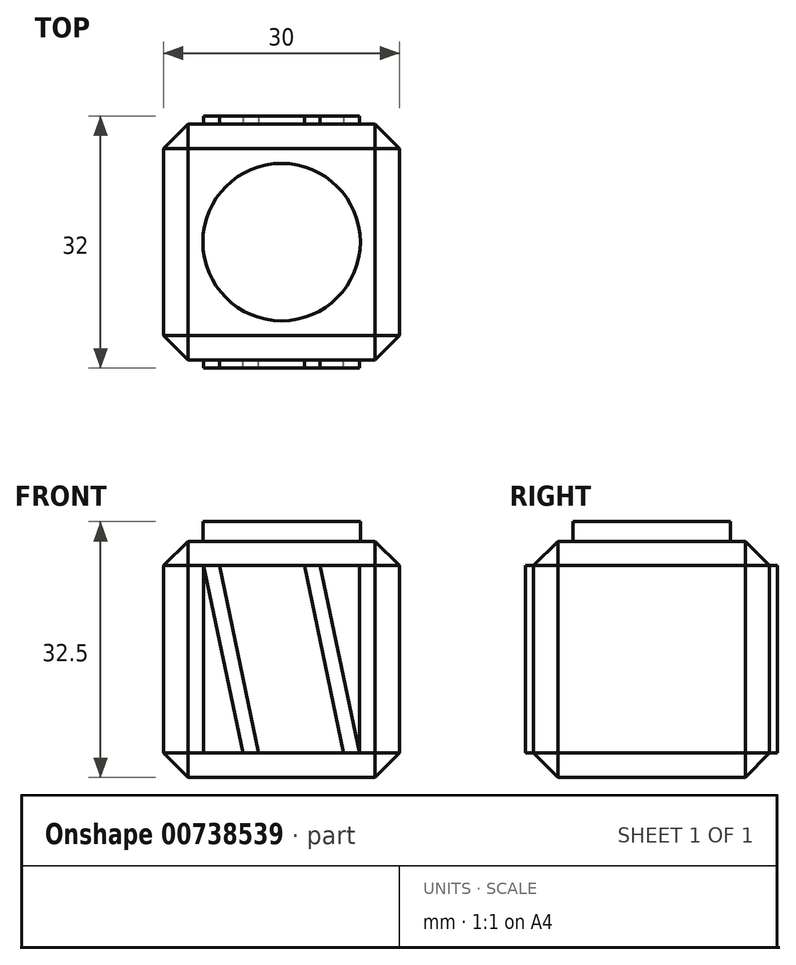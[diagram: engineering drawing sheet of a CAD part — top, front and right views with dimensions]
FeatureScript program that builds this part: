
annotation { "Feature Type Name" : "Feature", "Feature Type Description" : "" }
export const myFeature = defineFeature(function(context is Context, id is Id, definition is map)
    precondition{}
    {
        {
            var Q0;
            Q0=qCreatedBy(makeId("Top.planeOp"),FACE);
            var sketch = newSketch(context, id + "F0", { "sketchPlane" : qUnion([Q0])});
            skLineSegment(sketch, "E0", {"start": v(15, 15) * mm, "end": v(15, -15) * mm});
            skLineSegment(sketch, "E1", {"start": v(15, -15) * mm, "end": v(-15, -15) * mm});
            skLineSegment(sketch, "E2", {"start": v(-15, -15) * mm, "end": v(-15, 15) * mm});
            skLineSegment(sketch, "E3", {"start": v(-15, 15) * mm, "end": v(15, 15) * mm});
            skSolve(sketch);
        }
        {
            var Q0;
            Q0 = qSketchRegion(id + "F0", true);
            extrude(context, id + "F1", {"entities" : qUnion([Q0]), "depth" : 30 * mm, "offsetDistance" : 25 * mm});
        }
        {
            var Q0;
            Q0=makeQuery(id+"F1.opExtrude","CAP_EDGE",EDGE,{"disambiguationData":[OSD([sQuery(id+"F0.wireOp",EDGE,"E1")])],"isStart":false});
            var Q1;
            Q1=makeQuery(id+"F1.opExtrude","CAP_EDGE",EDGE,{"disambiguationData":[OSD([sQuery(id+"F0.wireOp",EDGE,"E0")])],"isStart":false});
            var Q2;
            Q2=makeQuery(id+"F1.opExtrude","SWEPT_EDGE",EDGE,{"disambiguationData":[OSD([sQuery(id+"F0.wireOp",EDGE,"E0"),sQuery(id+"F0.wireOp",EDGE,"E1")])]});
            var Q3;
            Q3=makeQuery(id+"F1.opExtrude","CAP_EDGE",EDGE,{"disambiguationData":[OSD([sQuery(id+"F0.wireOp",EDGE,"E2")])],"isStart":true});
            var Q4;
            Q4=makeQuery(id+"F1.opExtrude","CAP_EDGE",EDGE,{"disambiguationData":[OSD([sQuery(id+"F0.wireOp",EDGE,"E3")])],"isStart":true});
            var Q5;
            Q5=makeQuery(id+"F1.opExtrude","SWEPT_EDGE",EDGE,{"disambiguationData":[OSD([sQuery(id+"F0.wireOp",EDGE,"E2"),sQuery(id+"F0.wireOp",EDGE,"E3")])]});
            var Q6;
            Q6=makeQuery(id+"F1.opExtrude","CAP_EDGE",EDGE,{"disambiguationData":[OSD([sQuery(id+"F0.wireOp",EDGE,"E3")])],"isStart":false});
            var Q7;
            Q7=makeQuery(id+"F1.opExtrude","SWEPT_EDGE",EDGE,{"disambiguationData":[OSD([sQuery(id+"F0.wireOp",EDGE,"E0"),sQuery(id+"F0.wireOp",EDGE,"E3")])]});
            var Q8;
            Q8=makeQuery(id+"F1.opExtrude","SWEPT_EDGE",EDGE,{"disambiguationData":[OSD([sQuery(id+"F0.wireOp",EDGE,"E1"),sQuery(id+"F0.wireOp",EDGE,"E2")])]});
            var Q9;
            Q9=makeQuery(id+"F1.opExtrude","CAP_EDGE",EDGE,{"disambiguationData":[OSD([sQuery(id+"F0.wireOp",EDGE,"E1")])],"isStart":true});
            var Q10;
            Q10=makeQuery(id+"F1.opExtrude","CAP_EDGE",EDGE,{"disambiguationData":[OSD([sQuery(id+"F0.wireOp",EDGE,"E0")])],"isStart":true});
            var Q11;
            Q11=makeQuery(id+"F1.opExtrude","CAP_EDGE",EDGE,{"disambiguationData":[OSD([sQuery(id+"F0.wireOp",EDGE,"E2")])],"isStart":false});
            chamfer(context, id + "F2", {"entities" : qUnion([Q0, Q1, Q2, Q3, Q4, Q5, Q6, Q7, Q8, Q9, Q10, Q11]), "width" : 3.1 * mm, "tangentPropagation" : true});
        }
        {
            var Q0;
            Q0=qCreatedBy(makeId("Top.planeOp"),FACE);
            var sketch = newSketch(context, id + "F3", { "sketchPlane" : qUnion([Q0])});
            skCircle(sketch, "E4", {"center": v(0, 0) * mm, "radius": 10 * mm});
            skSolve(sketch);
        }
        {
            var Q0;
            Q0 = qSketchRegion(id + "F3", true);
            extrude(context, id + "F4", {"entities" : qUnion([Q0]), "operationType" : NewBodyOperationType.ADD, "depth" : 32.5 * mm, "offsetDistance" : 25 * mm});
        }
        {
            var Q0;
            Q0=makeQuery(id+"F1.opExtrude","SWEPT_FACE",FACE,{"disambiguationData":[OSD([sQuery(id+"F0.wireOp",EDGE,"E1")])]});
            var sketch = newSketch(context, id + "F5", { "sketchPlane" : qUnion([Q0])});
            skLineSegment(sketch, "E5", {"start": v(-9.9, 3.1) * mm, "end": v(-9.9, 26.9) * mm});
            skLineSegment(sketch, "E6", {"start": v(-9.9, 3.1) * mm, "end": v(-4.9, 3.1) * mm});
            skLineSegment(sketch, "E7", {"start": v(-4.9, 3.1) * mm, "end": v(-9.9, 26.9) * mm});
            skLineSegment(sketch, "E8", {"start": v(9.9, 26.9) * mm, "end": v(9.9, 3.1) * mm});
            skLineSegment(sketch, "E9", {"start": v(9.9, 26.9) * mm, "end": v(4.9, 26.9) * mm});
            skLineSegment(sketch, "E10", {"start": v(4.9, 26.9) * mm, "end": v(9.9, 3.1) * mm});
            skLineSegment(sketch, "E11", {"start": v(-2.9, 3.1) * mm, "end": v(-7.9, 26.9) * mm});
            skLineSegment(sketch, "E12", {"start": v(-7.9, 26.9) * mm, "end": v(2.9, 26.9) * mm});
            skLineSegment(sketch, "E13", {"start": v(2.9, 26.9) * mm, "end": v(7.9, 3.1) * mm});
            skLineSegment(sketch, "E14", {"start": v(-2.9, 3.1) * mm, "end": v(7.9, 3.1) * mm});
            skSolve(sketch);
        }
        {
            var Q0;
            Q0 = qSketchRegion(id + "F5", true);
            extrude(context, id + "F6", {"entities" : qUnion([Q0]), "operationType" : NewBodyOperationType.ADD, "depth" : 1 * mm, "offsetDistance" : 25 * mm});
        }
        {
            var Q0;
            Q0=makeQuery(id+"F1.opExtrude","SWEPT_FACE",FACE,{"disambiguationData":[OSD([sQuery(id+"F0.wireOp",EDGE,"E3")])]});
            var sketch = newSketch(context, id + "F7", { "sketchPlane" : qUnion([Q0])});
            skLineSegment(sketch, "E15", {"start": v(-9.9, 26.9) * mm, "end": v(-9.9, 3.1) * mm});
            skLineSegment(sketch, "E16", {"start": v(-9.9, 26.9) * mm, "end": v(-4.9, 26.9) * mm});
            skLineSegment(sketch, "E17", {"start": v(-4.9, 26.9) * mm, "end": v(-9.9, 3.1) * mm});
            skLineSegment(sketch, "E18", {"start": v(-7.9, 3.1) * mm, "end": v(-2.9, 26.9) * mm});
            skLineSegment(sketch, "E19", {"start": v(9.9, 26.9) * mm, "end": v(9.9, 3.1) * mm});
            skLineSegment(sketch, "E20", {"start": v(9.9, 3.1) * mm, "end": v(4.9, 3.1) * mm});
            skLineSegment(sketch, "E21", {"start": v(4.9, 3.1) * mm, "end": v(9.9, 26.9) * mm});
            skLineSegment(sketch, "E22", {"start": v(7.9, 26.9) * mm, "end": v(2.9, 3.1) * mm});
            skLineSegment(sketch, "E23", {"start": v(2.9, 3.1) * mm, "end": v(-7.9, 3.1) * mm});
            skLineSegment(sketch, "E24", {"start": v(-2.9, 26.9) * mm, "end": v(7.9, 26.9) * mm});
            skSolve(sketch);
        }
        {
            var Q0;
            Q0=makeQuery(id+"F7.imprint","IMPRINT",FACE,{"disambiguationData":[TD([[makeQuery(id+"F7.imprint","IMPRINT",EDGE,{"derivedFrom":sQuery(id+"F7.wireOp",EDGE,"E18")}),-1.0]])]});
            var Q1;
            Q1=makeQuery(id+"F7.imprint","IMPRINT",FACE,{"disambiguationData":[TD([[makeQuery(id+"F7.imprint","IMPRINT",EDGE,{"derivedFrom":sQuery(id+"F7.wireOp",EDGE,"E19")}),-1.0]])]});
            var Q2;
            Q2=makeQuery(id+"F7.imprint","IMPRINT",FACE,{"disambiguationData":[TD([[makeQuery(id+"F7.imprint","IMPRINT",EDGE,{"derivedFrom":sQuery(id+"F7.wireOp",EDGE,"E15")}),1.0]])]});
            extrude(context, id + "F8", {"entities" : qUnion([Q0, Q1, Q2]), "operationType" : NewBodyOperationType.ADD, "depth" : 1 * mm, "offsetDistance" : 25 * mm});
        }
    });
